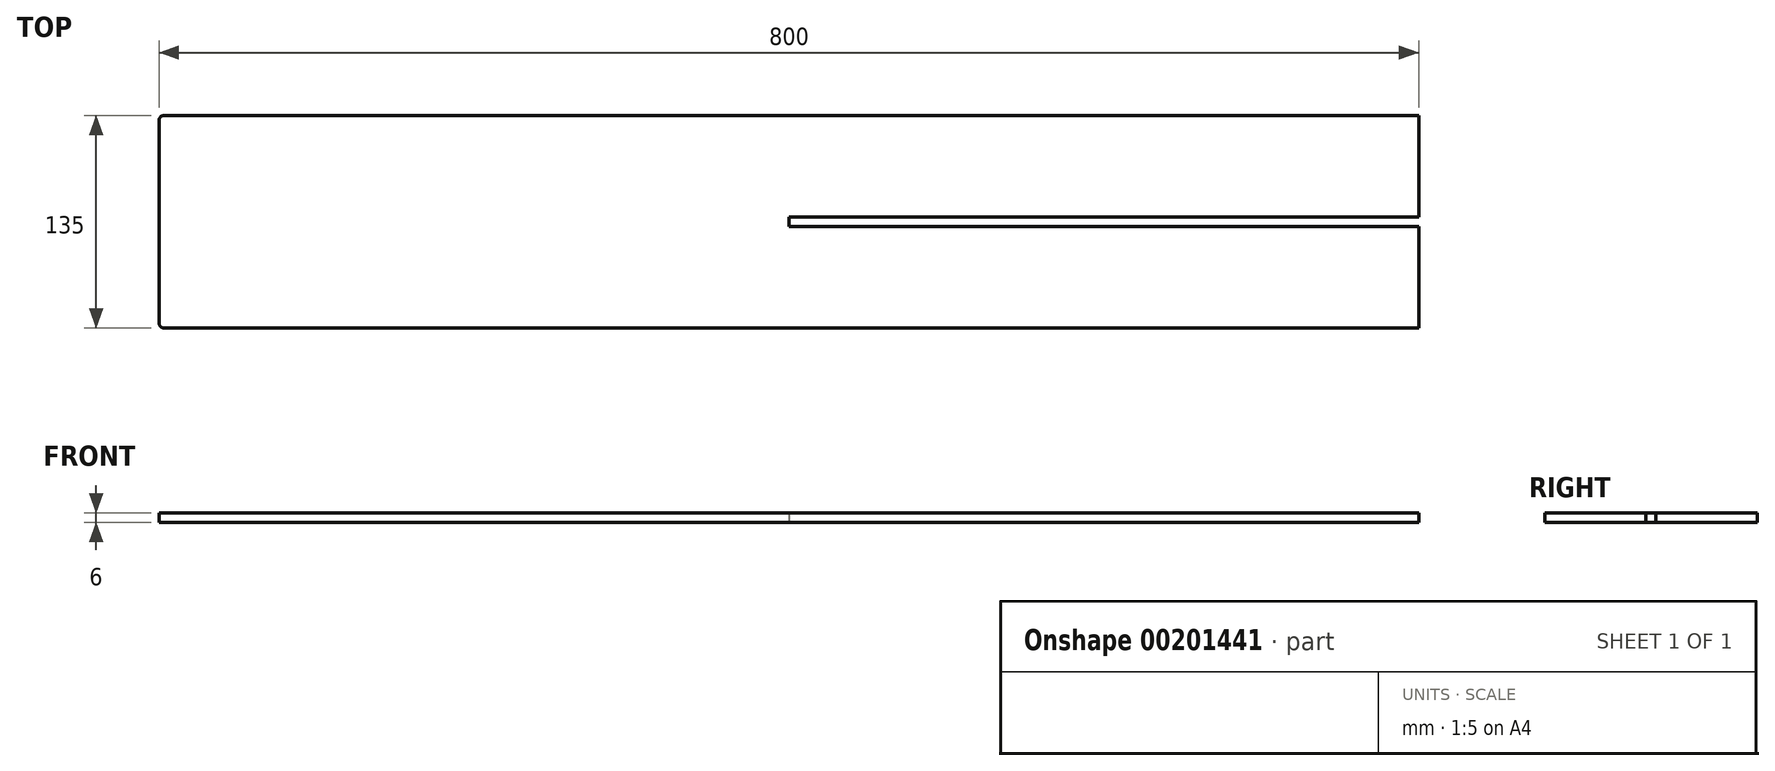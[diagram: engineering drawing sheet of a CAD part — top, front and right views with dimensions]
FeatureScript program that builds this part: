
annotation { "Feature Type Name" : "Feature", "Feature Type Description" : "" }
export const myFeature = defineFeature(function(context is Context, id is Id, definition is map)
    precondition{}
    {
        {
            var Q0;
            Q0=qCreatedBy(makeId("Top.planeOp"),FACE);
            var sketch = newSketch(context, id + "F0", { "sketchPlane" : qUnion([Q0])});
            skLineSegment(sketch, "E0.bottom", {"start": v(400, 70.6) * mm, "end": v(-397, 70.6) * mm});
            skLineSegment(sketch, "E0.top", {"start": v(400, -64.4) * mm, "end": v(-397, -64.4) * mm});
            skLineSegment(sketch, "E0.left", {"start": v(400, 70.6) * mm, "end": v(400, -64.4) * mm});
            skLineSegment(sketch, "E0.right", {"start": v(-400, 67.6) * mm, "end": v(-400, -61.4) * mm});
            skPoint(sketch, "E1.visualSharp", {"position": v(-400, 70.6) * mm});
            skArc(sketch, "E1.filletArc", {"start": v(-397, 70.6) * mm, "mid": v(-399.12, 69.72) * mm, "end": v(-400, 67.6) * mm});
            skPoint(sketch, "E2.visualSharp", {"position": v(-400, -64.4) * mm});
            skArc(sketch, "E2.filletArc", {"start": v(-400, -61.4) * mm, "mid": v(-399.12, -63.52) * mm, "end": v(-397, -64.4) * mm});
            skLineSegment(sketch, "E3", {"start": v(-400, 3.1) * mm, "end": v(-219.75, 3.1) * mm});
            skLineSegment(sketch, "E4", {"start": v(-219.75, 3.1) * mm, "end": v(438.28, 3.1) * mm});
            skLineSegment(sketch, "E5.bottom", {"start": v(0, 6.2) * mm, "end": v(400, 6.2) * mm});
            skLineSegment(sketch, "E5.top", {"start": v(0, 0) * mm, "end": v(400, 0) * mm});
            skLineSegment(sketch, "E5.left", {"start": v(0, 6.2) * mm, "end": v(0, 0) * mm});
            skLineSegment(sketch, "E5.right", {"start": v(400, 6.2) * mm, "end": v(400, 0) * mm});
            skLineSegment(sketch, "E6", {"start": v(0, 3.1) * mm, "end": v(400, 3.1) * mm});
            skSolve(sketch);
        }
        {
            var Q0;
            {var subQ4=sQuery(id+"F0.wireOp",EDGE,"E0.bottom");Q0=makeQuery(id+"F0.imprint","IMPRINT",FACE,{"disambiguationData":[TD([[makeQuery(id+"F0.imprint","IMPRINT",EDGE,{"derivedFrom":subQ4}),1.0]])]});}
            var Q1;
            {var subQ4=sQuery(id+"F0.wireOp",EDGE,"E0.top");Q1=makeQuery(id+"F0.imprint","IMPRINT",FACE,{"disambiguationData":[TD([[makeQuery(id+"F0.imprint","IMPRINT",EDGE,{"derivedFrom":subQ4}),-1.0]])]});}
            extrude(context, id + "F1", {"entities" : qUnion([Q0, Q1]), "depth" : 6 * mm});
        }
    });
